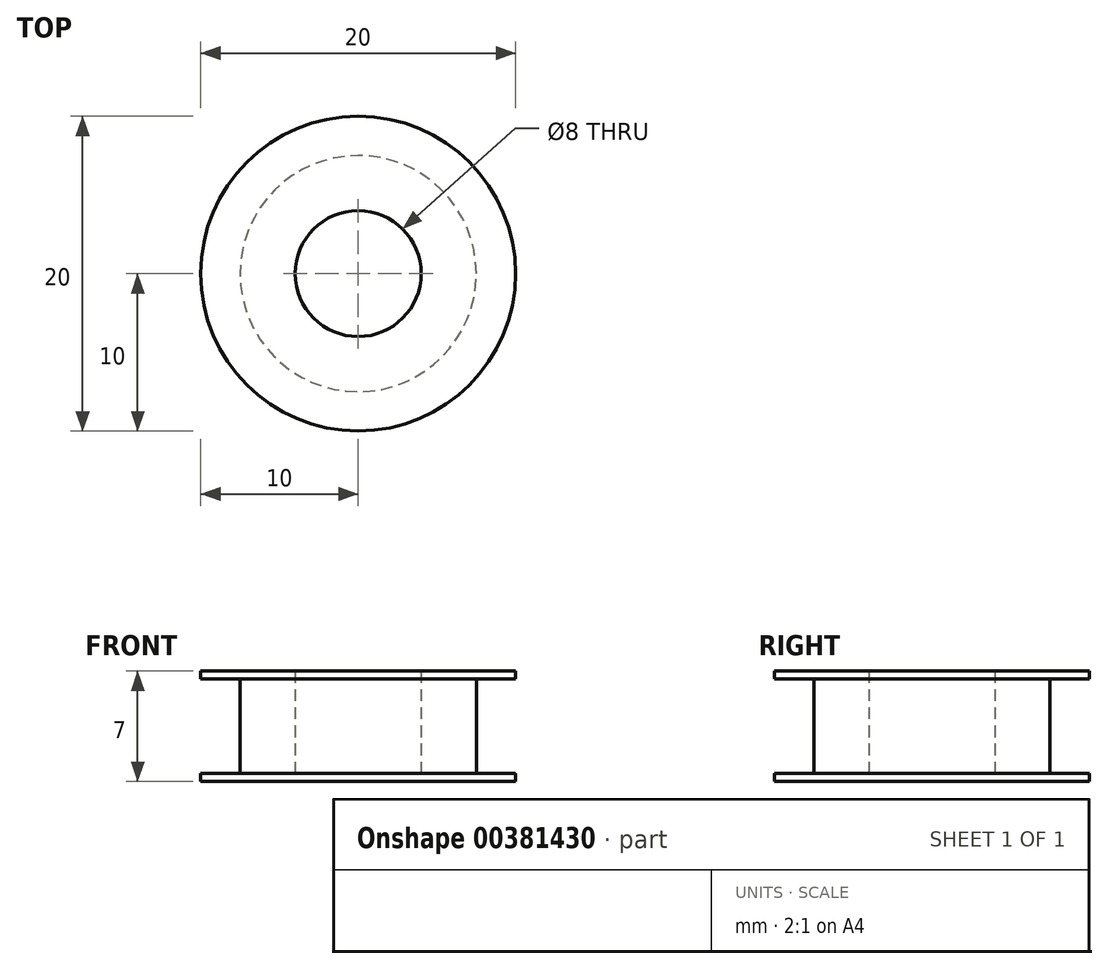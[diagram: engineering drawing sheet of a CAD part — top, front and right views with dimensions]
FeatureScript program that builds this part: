
annotation { "Feature Type Name" : "Feature", "Feature Type Description" : "" }
export const myFeature = defineFeature(function(context is Context, id is Id, definition is map)
    precondition{}
    {
        {
            var Q0;
            Q0=qCreatedBy(makeId("Top.planeOp"),FACE);
            var sketch = newSketch(context, id + "F0", { "sketchPlane" : qUnion([Q0])});
            skCircle(sketch, "E0", {"center": v(0, 0) * mm, "radius": 4 * mm});
            skCircle(sketch, "E1", {"center": v(0, 0) * mm, "radius": 7.5 * mm});
            skSolve(sketch);
        }
        {
            var Q0;
            Q0 = qSketchRegion(id + "F0", true);
            extrude(context, id + "F1", {"entities" : qUnion([Q0]), "depth" : 3 * mm});
        }
        {
            var Q0;
            Q0=makeQuery(id+"F1.opExtrude","CAP_FACE",FACE,{"disambiguationData":[OSD([sQuery(id+"F0.wireOp",EDGE,"E0"),sQuery(id+"F0.wireOp",EDGE,"E1")])],"isStart":false});
            var sketch = newSketch(context, id + "F2", { "sketchPlane" : qUnion([Q0])});
            skCircle(sketch, "E2", {"center": v(0, 0) * mm, "radius": 10 * mm});
            skSolve(sketch);
        }
        {
            var Q0;
            Q0=makeQuery(id+"F2.imprint","IMPRINT",FACE,{"disambiguationData":[TD([[makeQuery(id+"F2.imprint","IMPRINT",EDGE,{"derivedFrom":makeQuery(id+"F1.opExtrude","CAP_EDGE",EDGE,{"disambiguationData":[OSD([sQuery(id+"F0.wireOp",EDGE,"E0")])],"isStart":false})}),-1.0]])]});
            var Q1;
            Q1=makeQuery(id+"F2.imprint","IMPRINT",FACE,{"disambiguationData":[TD([[makeQuery(id+"F2.imprint","IMPRINT",EDGE,{"derivedFrom":sQuery(id+"F2.wireOp",EDGE,"E2")}),1.0]])]});
            extrude(context, id + "F3", {"entities" : qUnion([Q0, Q1]), "operationType" : NewBodyOperationType.ADD, "depth" : .5 * mm});
        }
        {
            var Q0;
            Q0=makeQuery(id+"F1.opExtrude","SWEPT_BODY",BODY,{"disambiguationData":[OSD([sQuery(id+"F0.wireOp",EDGE,"E0"),sQuery(id+"F0.wireOp",EDGE,"E1")])]});
            var Q1;
            Q1=makeQuery(id+"F1.opExtrude","CAP_FACE",FACE,{"disambiguationData":[OSD([sQuery(id+"F0.wireOp",EDGE,"E0"),sQuery(id+"F0.wireOp",EDGE,"E1")])],"isStart":true});
            mirror(context, id + "F4", {"operationType" : NewBodyOperationType.ADD, "entities" : qUnion([Q0]), "mirrorPlane" : qUnion([Q1])});
        }
    });
